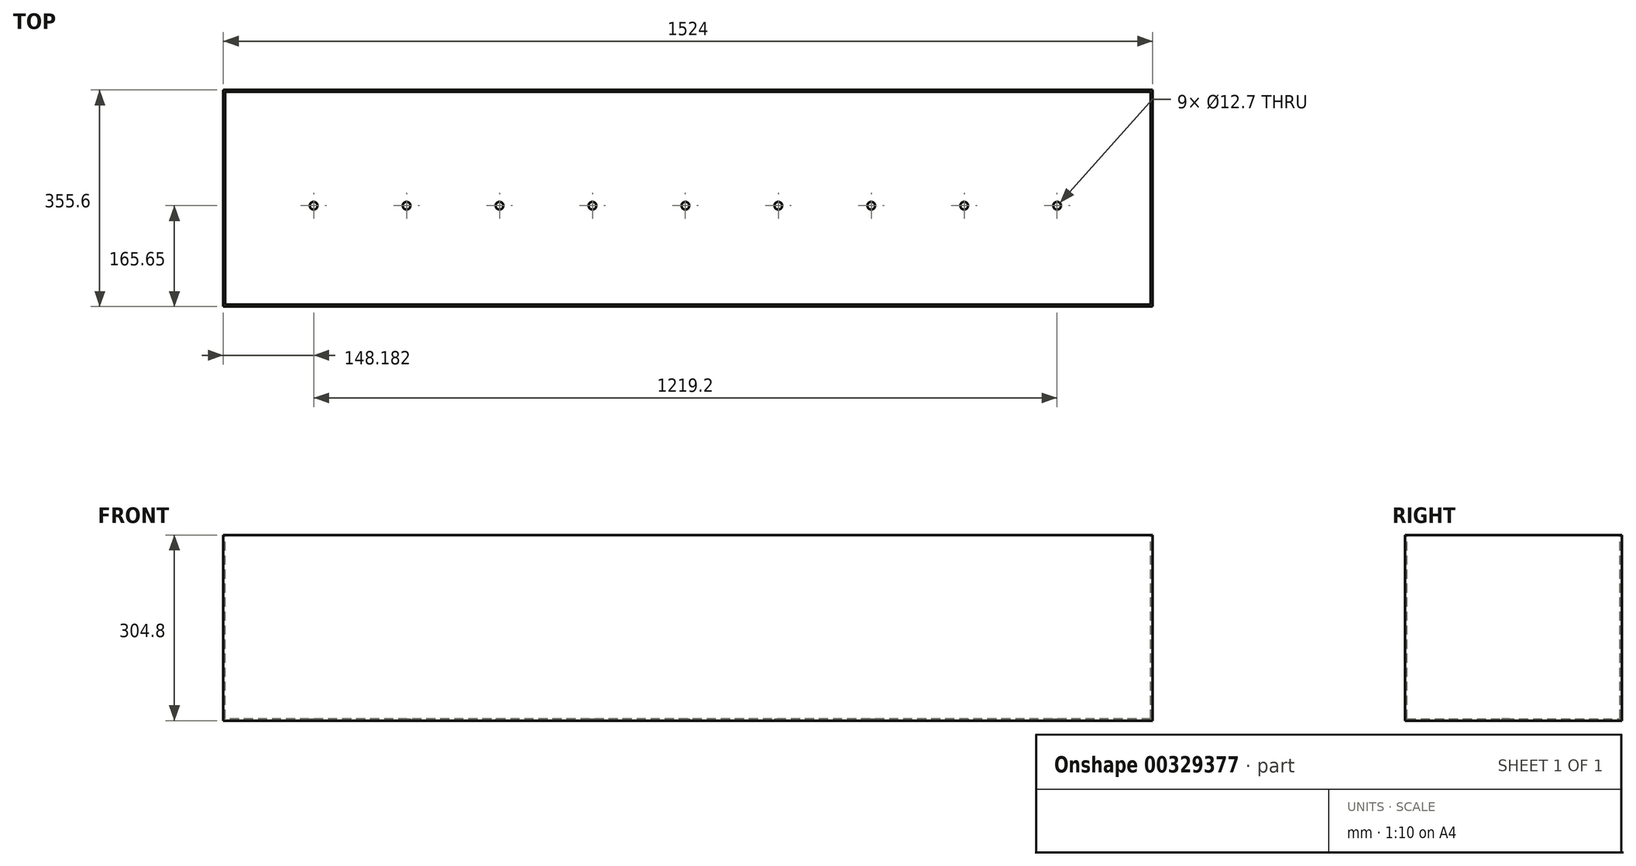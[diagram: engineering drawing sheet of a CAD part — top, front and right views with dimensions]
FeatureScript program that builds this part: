
annotation { "Feature Type Name" : "Feature", "Feature Type Description" : "" }
export const myFeature = defineFeature(function(context is Context, id is Id, definition is map)
    precondition{}
    {
        {
            var Q0;
            Q0=qCreatedBy(makeId("Front.planeOp"),FACE);
            var sketch = newSketch(context, id + "F0", { "sketchPlane" : qUnion([Q0])});
            skLineSegment(sketch, "E0.bottom", {"start": v(762, -152.4) * mm, "end": v(-762, -152.4) * mm});
            skLineSegment(sketch, "E0.top", {"start": v(762, 152.4) * mm, "end": v(-762, 152.4) * mm});
            skLineSegment(sketch, "E0.left", {"start": v(762, -152.4) * mm, "end": v(762, 152.4) * mm});
            skLineSegment(sketch, "E0.right", {"start": v(-762, -152.4) * mm, "end": v(-762, 152.4) * mm});
            skPoint(sketch, "E0.middle", {"position": v(0, 0) * mm});
            skSolve(sketch);
        }
        {
            var Q0;
            Q0=makeQuery(id+"F0.imprint","IMPRINT",FACE,{"disambiguationData":[TD([[makeQuery(id+"F0.imprint","IMPRINT",EDGE,{"derivedFrom":sQuery(id+"F0.wireOp",EDGE,"E0.bottom")}),-1.0]])]});
            extrude(context, id + "F1", {"entities" : qUnion([Q0]), "depth" : 355.6 * mm});
        }
        {
            var Q0;
            Q0=makeQuery(id+"F1.opExtrude","SWEPT_FACE",FACE,{"disambiguationData":[OSD([sQuery(id+"F0.wireOp",EDGE,"E0.top")])]});
            shell(context, id + "F2", {"entities" : qUnion([Q0]), "thickness" : 3.17 * mm});
        }
        {
            var Q0;
            Q0=makeQuery(id+"F1.opExtrude","SWEPT_FACE",FACE,{"disambiguationData":[OSD([sQuery(id+"F0.wireOp",EDGE,"E0.bottom")])]});
            var sketch = newSketch(context, id + "F3", { "sketchPlane" : qUnion([Q0])});
            skCircle(sketch, "E1", {"center": v(-613.82, 189.95) * mm, "radius": 6.35 * mm});
            skCircle(sketch, "E2.1.0.0", {"center": v(-461.42, 189.95) * mm, "radius": 6.35 * mm});
            skCircle(sketch, "E2.2.0.0", {"center": v(-309.02, 189.95) * mm, "radius": 6.35 * mm});
            skCircle(sketch, "E2.3.0.0", {"center": v(-156.62, 189.95) * mm, "radius": 6.35 * mm});
            skCircle(sketch, "E2.4.0.0", {"center": v(-4.22, 189.95) * mm, "radius": 6.35 * mm});
            skCircle(sketch, "E2.5.0.0", {"center": v(148.18, 189.95) * mm, "radius": 6.35 * mm});
            skCircle(sketch, "E2.6.0.0", {"center": v(300.58, 189.95) * mm, "radius": 6.35 * mm});
            skCircle(sketch, "E2.7.0.0", {"center": v(452.98, 189.95) * mm, "radius": 6.35 * mm});
            skLineSegment(sketch, "E2.direction1", {"start": v(-613.82, 189.95) * mm, "end": v(-461.42, 189.95) * mm, "construction": true});
            skCircle(sketch, "E3.0.8.0", {"center": v(605.38, 189.95) * mm, "radius": 6.35 * mm});
            skSolve(sketch);
        }
        {
            var Q0;
            Q0=makeQuery(id+"F3.imprint","IMPRINT",FACE,{"disambiguationData":[TD([[makeQuery(id+"F3.imprint","IMPRINT",EDGE,{"derivedFrom":sQuery(id+"F3.wireOp",EDGE,"E1")}),1.0]])]});
            var Q1;
            Q1=makeQuery(id+"F3.imprint","IMPRINT",FACE,{"disambiguationData":[TD([[makeQuery(id+"F3.imprint","IMPRINT",EDGE,{"derivedFrom":sQuery(id+"F3.wireOp",EDGE,"E2.1.0.0")}),1.0]])]});
            var Q2;
            Q2=makeQuery(id+"F3.imprint","IMPRINT",FACE,{"disambiguationData":[TD([[makeQuery(id+"F3.imprint","IMPRINT",EDGE,{"derivedFrom":sQuery(id+"F3.wireOp",EDGE,"E2.2.0.0")}),1.0]])]});
            var Q3;
            Q3=makeQuery(id+"F3.imprint","IMPRINT",FACE,{"disambiguationData":[TD([[makeQuery(id+"F3.imprint","IMPRINT",EDGE,{"derivedFrom":sQuery(id+"F3.wireOp",EDGE,"E2.3.0.0")}),1.0]])]});
            var Q4;
            Q4=makeQuery(id+"F3.imprint","IMPRINT",FACE,{"disambiguationData":[TD([[makeQuery(id+"F3.imprint","IMPRINT",EDGE,{"derivedFrom":sQuery(id+"F3.wireOp",EDGE,"E2.4.0.0")}),1.0]])]});
            var Q5;
            Q5=makeQuery(id+"F3.imprint","IMPRINT",FACE,{"disambiguationData":[TD([[makeQuery(id+"F3.imprint","IMPRINT",EDGE,{"derivedFrom":sQuery(id+"F3.wireOp",EDGE,"E2.5.0.0")}),1.0]])]});
            var Q6;
            Q6=makeQuery(id+"F3.imprint","IMPRINT",FACE,{"disambiguationData":[TD([[makeQuery(id+"F3.imprint","IMPRINT",EDGE,{"derivedFrom":sQuery(id+"F3.wireOp",EDGE,"E2.6.0.0")}),1.0]])]});
            var Q7;
            Q7=makeQuery(id+"F3.imprint","IMPRINT",FACE,{"disambiguationData":[TD([[makeQuery(id+"F3.imprint","IMPRINT",EDGE,{"derivedFrom":sQuery(id+"F3.wireOp",EDGE,"E2.7.0.0")}),1.0]])]});
            var Q8;
            Q8=makeQuery(id+"F3.imprint","IMPRINT",FACE,{"disambiguationData":[TD([[makeQuery(id+"F3.imprint","IMPRINT",EDGE,{"derivedFrom":sQuery(id+"F3.wireOp",EDGE,"E3.0.8.0")}),1.0]])]});
            extrude(context, id + "F4", {"entities" : qUnion([Q0, Q1, Q2, Q3, Q4, Q5, Q6, Q7, Q8]), "operationType" : NewBodyOperationType.REMOVE, "oppositeDirection" : true, "depth" : 25.4 * mm});
        }
    });
